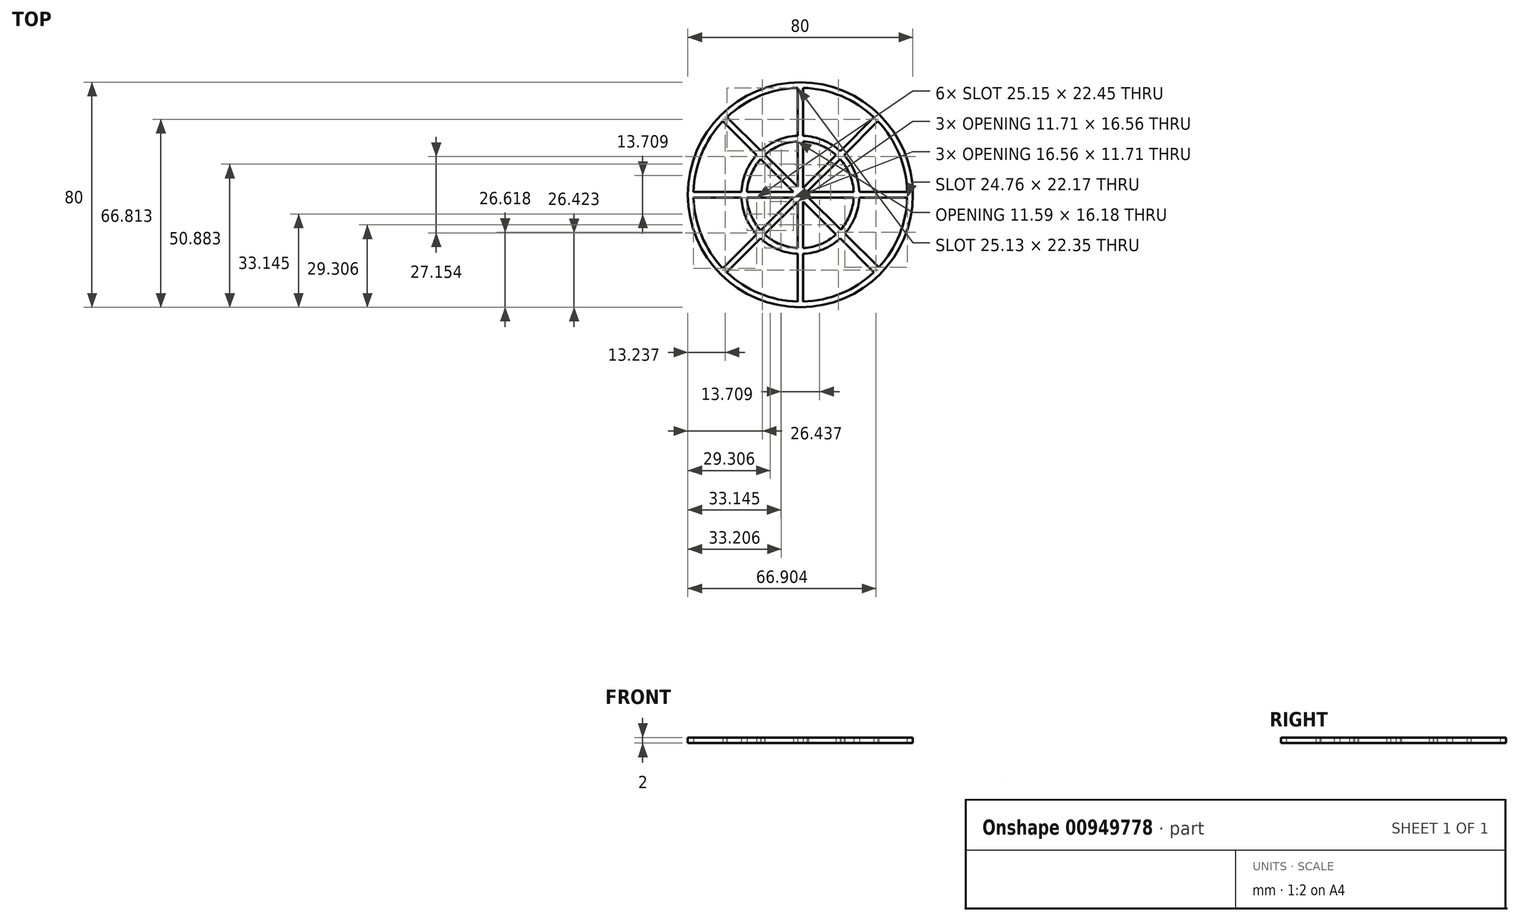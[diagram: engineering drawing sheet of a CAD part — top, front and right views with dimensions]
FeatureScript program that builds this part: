
annotation { "Feature Type Name" : "Feature", "Feature Type Description" : "" }
export const myFeature = defineFeature(function(context is Context, id is Id, definition is map)
    precondition{}
    {
        {
            var Q0;
            Q0=qCreatedBy(makeId("Top.planeOp"),FACE);
            var sketch = newSketch(context, id + "F0", { "sketchPlane" : qUnion([Q0])});
            skCircle(sketch, "E0", {"center": v(0, 0) * mm, "radius": 40 * mm});
            skArc(sketch, "E1.0", {"start": v(37.99, 1) * mm, "mid": v(35.1, 14.54) * mm, "end": v(27.57, 26.15) * mm});
            skLineSegment(sketch, "E2.left", {"start": v(-1, 37.99) * mm, "end": v(-1, 20.98) * mm});
            skLineSegment(sketch, "E2.right", {"start": v(1, 37.99) * mm, "end": v(1, 20.98) * mm});
            skLineSegment(sketch, "E3.bottom", {"start": v(37.99, 1) * mm, "end": v(20.98, 1) * mm});
            skLineSegment(sketch, "E4.trimOffspring", {"start": v(37.99, -1) * mm, "end": v(20.98, -1) * mm});
            skLineSegment(sketch, "E5.trimOffspring", {"start": v(1, -2.41) * mm, "end": v(1, -18.97) * mm});
            skLineSegment(sketch, "E6.trimOffspring", {"start": v(-2.41, 1) * mm, "end": v(-18.97, 1) * mm});
            skLineSegment(sketch, "E7.trimOffspring", {"start": v(-1, -2.41) * mm, "end": v(-1, -18.97) * mm});
            skLineSegment(sketch, "E8.trimOffspring", {"start": v(-2.41, -1) * mm, "end": v(-18.97, -1) * mm});
            skArc(sketch, "E9.trimOffspring", {"start": v(-37.99, -1) * mm, "mid": v(-35.1, -14.54) * mm, "end": v(-27.57, -26.15) * mm});
            skArc(sketch, "E10.trimOffspring", {"start": v(1, -37.99) * mm, "mid": v(14.54, -35.1) * mm, "end": v(26.15, -27.57) * mm});
            skPoint(sketch, "E2.bottom.end.orphan", {"position": v(1, 42.39) * mm});
            skPoint(sketch, "E11.orphan", {"position": v(-1, 42.39) * mm});
            skArc(sketch, "E12.trimOffspring", {"start": v(-1, 37.99) * mm, "mid": v(-14.52, 35.11) * mm, "end": v(-26.13, 27.6) * mm});
            skLineSegment(sketch, "E13", {"start": v(27.57, 26.15) * mm, "end": v(15.54, 14.13) * mm});
            skLineSegment(sketch, "E14", {"start": v(-27.57, -26.15) * mm, "end": v(-15.54, -14.13) * mm});
            skArc(sketch, "E15.trimOffspring", {"start": v(26.15, 27.57) * mm, "mid": v(14.54, 35.1) * mm, "end": v(1, 37.99) * mm});
            skLineSegment(sketch, "E16", {"start": v(26.15, -27.57) * mm, "end": v(14.13, -15.54) * mm});
            skLineSegment(sketch, "E17", {"start": v(27.93, -25.76) * mm, "end": v(15.82, -13.81) * mm});
            skArc(sketch, "E18.trimOffspring", {"start": v(-27.57, 26.15) * mm, "mid": v(-35.1, 14.54) * mm, "end": v(-37.99, 1) * mm});
            skLineSegment(sketch, "E19.trimOffspring", {"start": v(1, 2.41) * mm, "end": v(12.7, 14.12) * mm});
            skLineSegment(sketch, "E20.trimOffspring", {"start": v(-1, 2.8) * mm, "end": v(-12.59, 14.23) * mm});
            skLineSegment(sketch, "E21.trimOffspring", {"start": v(-2.41, 1) * mm, "end": v(-27.57, 26.15) * mm});
            skLineSegment(sketch, "E22.trimOffspring", {"start": v(-1, -2.41) * mm, "end": v(-12.7, -14.12) * mm});
            skArc(sketch, "E23.trimOffspring", {"start": v(-26.15, -27.57) * mm, "mid": v(-14.54, -35.1) * mm, "end": v(-1, -37.99) * mm});
            skArc(sketch, "E24.trimOffspring", {"start": v(27.93, -25.76) * mm, "mid": v(35.2, -14.3) * mm, "end": v(37.99, -1) * mm});
            skArc(sketch, "E25", {"start": v(-14.12, 12.7) * mm, "mid": v(-17.55, 7.27) * mm, "end": v(-18.97, 1) * mm});
            skArc(sketch, "E26.0", {"start": v(-15.54, 14.13) * mm, "mid": v(-19.4, 8.04) * mm, "end": v(-20.98, 1) * mm});
            skLineSegment(sketch, "E27.trimOffspring", {"start": v(-14.02, 15.64) * mm, "end": v(-26.13, 27.6) * mm});
            skArc(sketch, "E28.trimOffspring", {"start": v(-1, 20.98) * mm, "mid": v(-7.97, 19.43) * mm, "end": v(-14.02, 15.64) * mm});
            skLineSegment(sketch, "E29.trimOffspring", {"start": v(1, 18.97) * mm, "end": v(1, 2.41) * mm});
            skArc(sketch, "E30.trimOffspring", {"start": v(-1, 18.97) * mm, "mid": v(-7.2, 17.58) * mm, "end": v(-12.59, 14.23) * mm});
            skLineSegment(sketch, "E31.trimOffspring", {"start": v(-1, 18.97) * mm, "end": v(-1, 2.8) * mm});
            skArc(sketch, "E32.trimOffspring", {"start": v(14.13, 15.54) * mm, "mid": v(8.04, 19.4) * mm, "end": v(1, 20.98) * mm});
            skArc(sketch, "E33.trimOffspring", {"start": v(12.7, 14.12) * mm, "mid": v(7.27, 17.55) * mm, "end": v(1, 18.97) * mm});
            skLineSegment(sketch, "E34.trimOffspring", {"start": v(14.12, 12.7) * mm, "end": v(2.41, 1) * mm});
            skLineSegment(sketch, "E35.trimOffspring", {"start": v(14.13, 15.54) * mm, "end": v(26.15, 27.57) * mm});
            skLineSegment(sketch, "E36.trimOffspring", {"start": v(18.97, 1) * mm, "end": v(2.41, 1) * mm});
            skLineSegment(sketch, "E37.trimOffspring", {"start": v(18.97, -1) * mm, "end": v(2.84, -1) * mm});
            skArc(sketch, "E38.trimOffspring", {"start": v(18.97, 1) * mm, "mid": v(17.55, 7.27) * mm, "end": v(14.12, 12.7) * mm});
            skArc(sketch, "E39.trimOffspring", {"start": v(20.98, 1) * mm, "mid": v(19.4, 8.04) * mm, "end": v(15.54, 14.13) * mm});
            skLineSegment(sketch, "E40.trimOffspring", {"start": v(-14.12, -12.7) * mm, "end": v(-2.41, -1) * mm});
            skArc(sketch, "E41.trimOffspring", {"start": v(-12.7, -14.12) * mm, "mid": v(-7.27, -17.55) * mm, "end": v(-1, -18.97) * mm});
            skArc(sketch, "E42.trimOffspring", {"start": v(-14.13, -15.54) * mm, "mid": v(-8.04, -19.4) * mm, "end": v(-1, -20.98) * mm});
            skLineSegment(sketch, "E43.trimOffspring", {"start": v(-14.13, -15.54) * mm, "end": v(-26.15, -27.57) * mm});
            skLineSegment(sketch, "E44.trimOffspring", {"start": v(14.4, -12.4) * mm, "end": v(2.84, -1) * mm});
            skLineSegment(sketch, "E45.trimOffspring", {"start": v(12.7, -14.12) * mm, "end": v(1, -2.41) * mm});
            skArc(sketch, "E46.trimOffspring", {"start": v(14.4, -12.4) * mm, "mid": v(17.63, -7.08) * mm, "end": v(18.97, -1) * mm});
            skArc(sketch, "E47.trimOffspring", {"start": v(15.82, -13.81) * mm, "mid": v(19.48, -7.84) * mm, "end": v(20.98, -1) * mm});
            skArc(sketch, "E48.trimOffspring", {"start": v(1, -18.97) * mm, "mid": v(7.27, -17.55) * mm, "end": v(12.7, -14.12) * mm});
            skLineSegment(sketch, "E49.trimOffspring", {"start": v(1, -20.98) * mm, "end": v(1, -37.99) * mm});
            skLineSegment(sketch, "E50.trimOffspring", {"start": v(-1, -20.98) * mm, "end": v(-1, -37.99) * mm});
            skArc(sketch, "E51.trimOffspring", {"start": v(1, -20.98) * mm, "mid": v(8.04, -19.4) * mm, "end": v(14.13, -15.54) * mm});
            skLineSegment(sketch, "E52.trimOffspring", {"start": v(-20.98, 1) * mm, "end": v(-37.99, 1) * mm});
            skLineSegment(sketch, "E53.trimOffspring", {"start": v(-20.98, -1) * mm, "end": v(-37.99, -1) * mm});
            skArc(sketch, "E54.trimOffspring", {"start": v(-18.97, -1) * mm, "mid": v(-17.55, -7.27) * mm, "end": v(-14.12, -12.7) * mm});
            skArc(sketch, "E55.trimOffspring", {"start": v(-20.98, -1) * mm, "mid": v(-19.4, -8.04) * mm, "end": v(-15.54, -14.13) * mm});
            skSolve(sketch);
        }
        {
            var Q0;
            Q0 = qSketchRegion(id + "F0", true);
            extrude(context, id + "F1", {"entities" : qUnion([Q0]), "depth" : 2 * mm, "offsetDistance" : 25 * mm});
        }
    });
